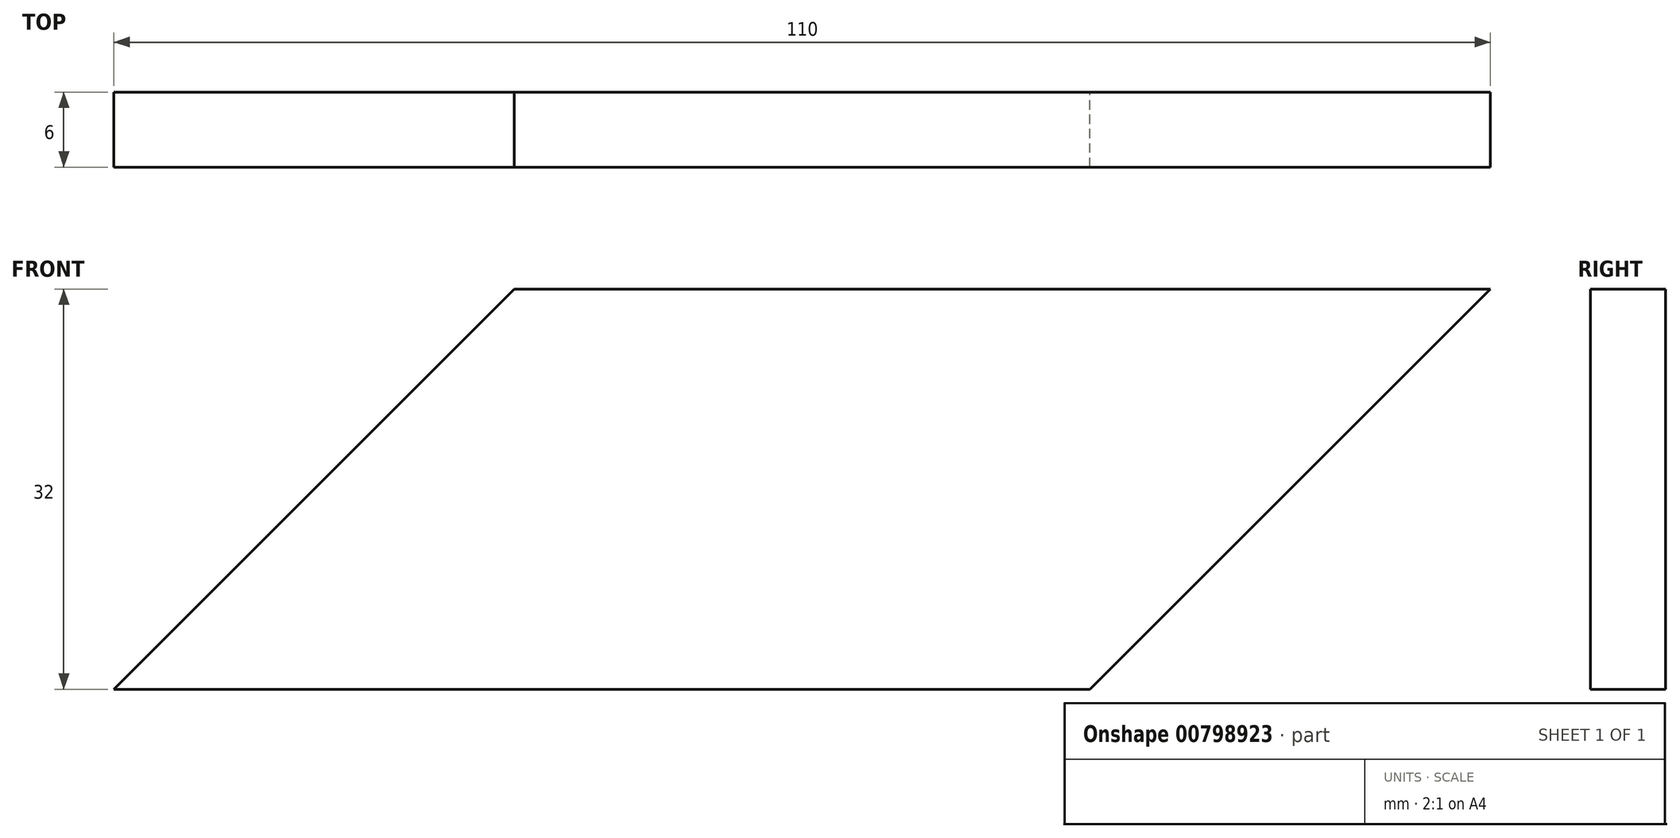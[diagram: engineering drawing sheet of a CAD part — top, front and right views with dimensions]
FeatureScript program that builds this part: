
annotation { "Feature Type Name" : "Feature", "Feature Type Description" : "" }
export const myFeature = defineFeature(function(context is Context, id is Id, definition is map)
    precondition{}
    {
        {
            var Q0;
            Q0=qCreatedBy(makeId("Front.planeOp"),FACE);
            var sketch = newSketch(context, id + "F0", { "sketchPlane" : qUnion([Q0])});
            skLineSegment(sketch, "E0", {"start": v(0, 0) * mm, "end": v(110, 0) * mm});
            skLineSegment(sketch, "E1", {"start": v(110, 0) * mm, "end": v(110, 32) * mm});
            skLineSegment(sketch, "E2", {"start": v(110, 32) * mm, "end": v(78, 0) * mm});
            skLineSegment(sketch, "E3", {"start": v(0, 0) * mm, "end": v(32, 32) * mm});
            skLineSegment(sketch, "E4", {"start": v(32, 32) * mm, "end": v(110, 32) * mm});
            skSolve(sketch);
        }
        {
            var Q0;
            {var subQ2=sQuery(id+"F0.wireOp",EDGE,"E2");Q0=makeQuery(id+"F0.imprint","IMPRINT",FACE,{"disambiguationData":[TD([[makeQuery(id+"F0.imprint","IMPRINT",EDGE,{"derivedFrom":subQ2}),-1.0]])]});}
            extrude(context, id + "F1", {"entities" : qUnion([Q0]), "endBound" : BoundingType.SYMMETRIC, "depth" : 6 * mm});
        }
    });
